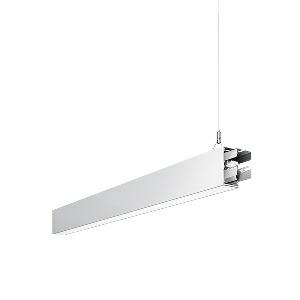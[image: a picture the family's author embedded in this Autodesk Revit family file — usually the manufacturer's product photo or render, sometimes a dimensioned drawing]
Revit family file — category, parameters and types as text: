
# Revit family: idoo_line_-_ilp_4000_840_d_mid_00805697_b92b
name_source: partatom
category: Lighting Fixtures
units: mm (PartAtom-declared; Revit-internal decimal feet)

## family parameters
Cut with Voids When Loaded = No
Host = Face
Light Source = No
Part Type = Normal
Room Calculation Point = No
Round Connector Dimension = Use Diameter
Shared = No

## types (1)
- IDOO.line - ILP 4000/840/D MID (1 x LED, 3950 lm, 4000K)
    Apparent Load = 29 VA
    Approval mark = CE
    CIE Flux Codes = 66 91 98 40 100
    Color Rendering = 80-89
    Color Temperature = 4000K
    Control Gear = Electronic ballast
    Default Elevation = 1800 mm
    Description = ILP 4000/840/D|Suspended luminaire|light source: LED|connected load: 220-240 V, 50/60 Hz|Power consumption: approx. 29 W|standby: approx. 0,15|luminous flux: 3950 lm|luminous efficacy: 136 lm/W|light distribution: Direct/indirect|direct ratio: approx. 40 %|colour temperature: Cold white, ca. 4000 K|color rendering index (CRI): >= 80|chromaticity tolerance:  3 SDCM|System of protection: IP 40|technology: Continuously dimmable|luminaire body|material: Sectional aluminium|colour: White|lamp cover: Acrylic (PMMA), Clear|mains lead: 1,0 m With free stranded wires|Fastening: Steel cable 0.3 - 0.7 m|glare control: Prism aperture|luminance(L65): <= 2700 cd/m|unified glare rating(4H 8H): <=  16|special features: DALI Load 1x, TouchDIM - dimming via standard switch, Through-wired, up to 18 m on one mains connection, Flicker-free, Suitable as emergency lighting, Mechanical and electrical connection of the individual modules without tools|
    Frequency = 50 Hz
    Height = 110 mm
    Lamp = 1 x LED
    Lamp Light Flux = 3950 lm
    Lamp count = 1
    Length = 1402 mm
    Luminous efficacy = 136 lm/W
    Manufacturer = Waldmann
    ModVariant = No
    Model = 00805697
    Mounting Place = Ceiling
    Mounting Type = Pendant
    Number of Poles = 1
    OnlyDefault = Yes
    Power Factor = 1
    Product Name = IDOO.line - ILP 4000/840/D MID
    Product group = Suspended luminaire
    ProductGroupID = 9
    Protection Class = Protection class I
    Protection Degree = IP 40
    RLX_Detail_Level = 1
    RLX_Emergency_Light_Flux = 0 lm
    RLX_Emergency_Type = 0
    RLX_Emergency_Type_DB = No
    RlxData = <blob elided: 20321 chars, md5=110d795f>
    Socket = socket
    Standby Power = 0 W
    System Light Flux = 3950 lm
    System Power = 29 W
    Type Comments = Product without accessories
    Type Image = 113308000-00692588.jpg
    URL = http://relux.com
    VarID = ---
    Voltage = 230 V
    Voltage Range = 220-240 V
    Weight = 0.00 kg
    Width = 60 mm  [stored 0.19685 ft]

note: [stored X ft] marks values corroborated as IEEE doubles in the binary element streams (Revit-internal decimal feet)

## geometry (parser evidence)
native form markers: Blend x4, Sweep x13
no freeform markers — native parametric forms only
